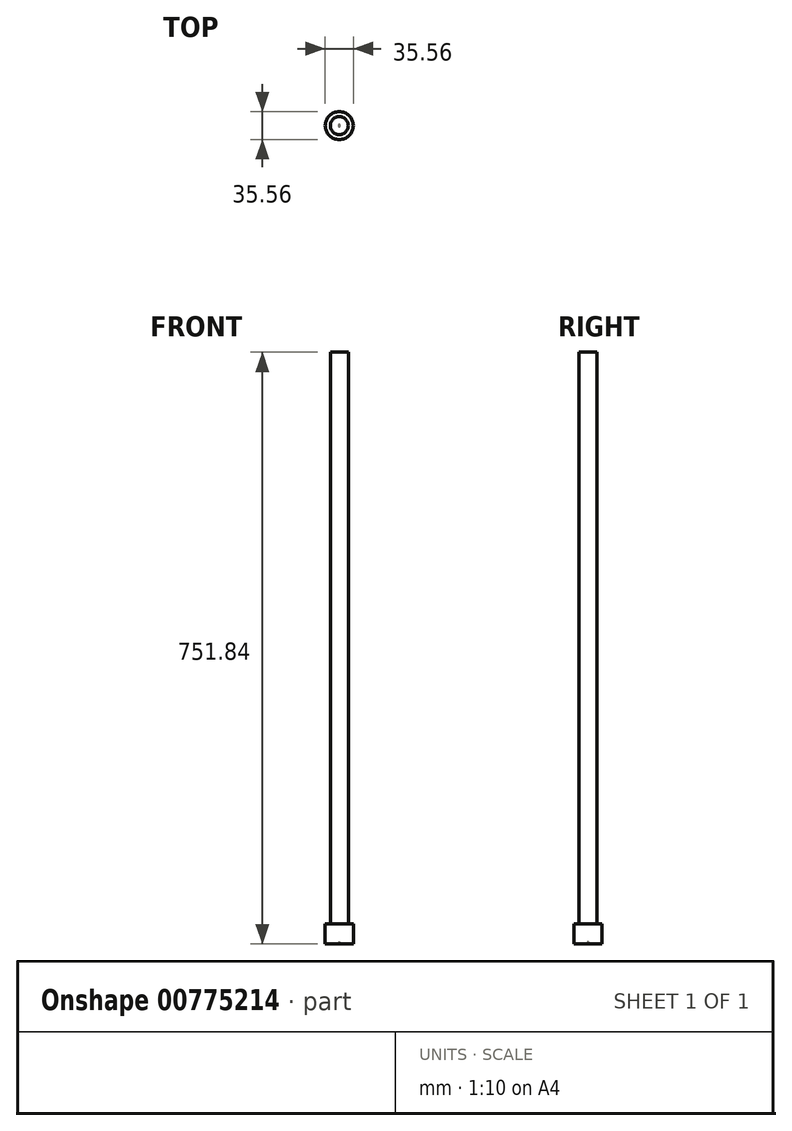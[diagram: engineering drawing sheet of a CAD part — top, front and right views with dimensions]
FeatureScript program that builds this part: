
annotation { "Feature Type Name" : "Feature", "Feature Type Description" : "" }
export const myFeature = defineFeature(function(context is Context, id is Id, definition is map)
    precondition{}
    {
        {
            var Q0;
            Q0=qCreatedBy(makeId("Top.planeOp"),FACE);
            var sketch = newSketch(context, id + "F0", { "sketchPlane" : qUnion([Q0])});
            skCircle(sketch, "E0", {"center": v(0, 0) * mm, "radius": 11.43 * mm});
            skSolve(sketch);
        }
        {
            var Q0;
            Q0 = qSketchRegion(id + "F0", true);
            extrude(context, id + "F1", {"entities" : qUnion([Q0]), "depth" : 774.7 * mm, "offsetDistance" : 25.4 * mm});
        }
        {
            var Q0;
            Q0=makeQuery(id+"F1.opExtrude","CAP_FACE",FACE,{"disambiguationData":[OSD([sQuery(id+"F0.wireOp",EDGE,"E0")])],"isStart":true});
            var sketch = newSketch(context, id + "F2", { "sketchPlane" : qUnion([Q0])});
            skCircle(sketch, "E1", {"center": v(0, 0) * mm, "radius": 17.78 * mm});
            skSolve(sketch);
        }
        {
            var Q0;
            Q0 = qSketchRegion(id + "F2", true);
            extrude(context, id + "F3", {"entities" : qUnion([Q0]), "operationType" : NewBodyOperationType.ADD, "depth" : 25.4 * mm, "offsetDistance" : 25.4 * mm});
        }
        {
            var Q0;
            Q0=makeQuery(id+"F1.opExtrude","CAP_FACE",FACE,{"disambiguationData":[OSD([sQuery(id+"F0.wireOp",EDGE,"E0")])],"isStart":false});
            extrude(context, id + "F4", {"entities" : qUnion([Q0]), "operationType" : NewBodyOperationType.REMOVE, "oppositeDirection" : true, "depth" : 48.26 * mm, "offsetDistance" : 25.4 * mm});
        }
        {
            var Q0;
            Q0=makeQuery(id+"F3.opExtrude","CAP_FACE",FACE,{"disambiguationData":[OSD([sQuery(id+"F2.wireOp",EDGE,"E1")])],"isStart":false});
            var sketch = newSketch(context, id + "F5", { "sketchPlane" : qUnion([Q0])});
            skCircle(sketch, "E2", {"center": v(0, 0) * mm, "radius": 1.27 * mm});
            skSolve(sketch);
        }
        {
            var Q0;
            Q0 = qSketchRegion(id + "F5", true);
            extrude(context, id + "F6", {"entities" : qUnion([Q0]), "operationType" : NewBodyOperationType.REMOVE, "oppositeDirection" : true, "depth" : 2.54 * mm, "offsetDistance" : 25.4 * mm, "hasDraft" : true, "draftAngle" : 15 * degree, "draftPullDirection" : true});
        }
    });
